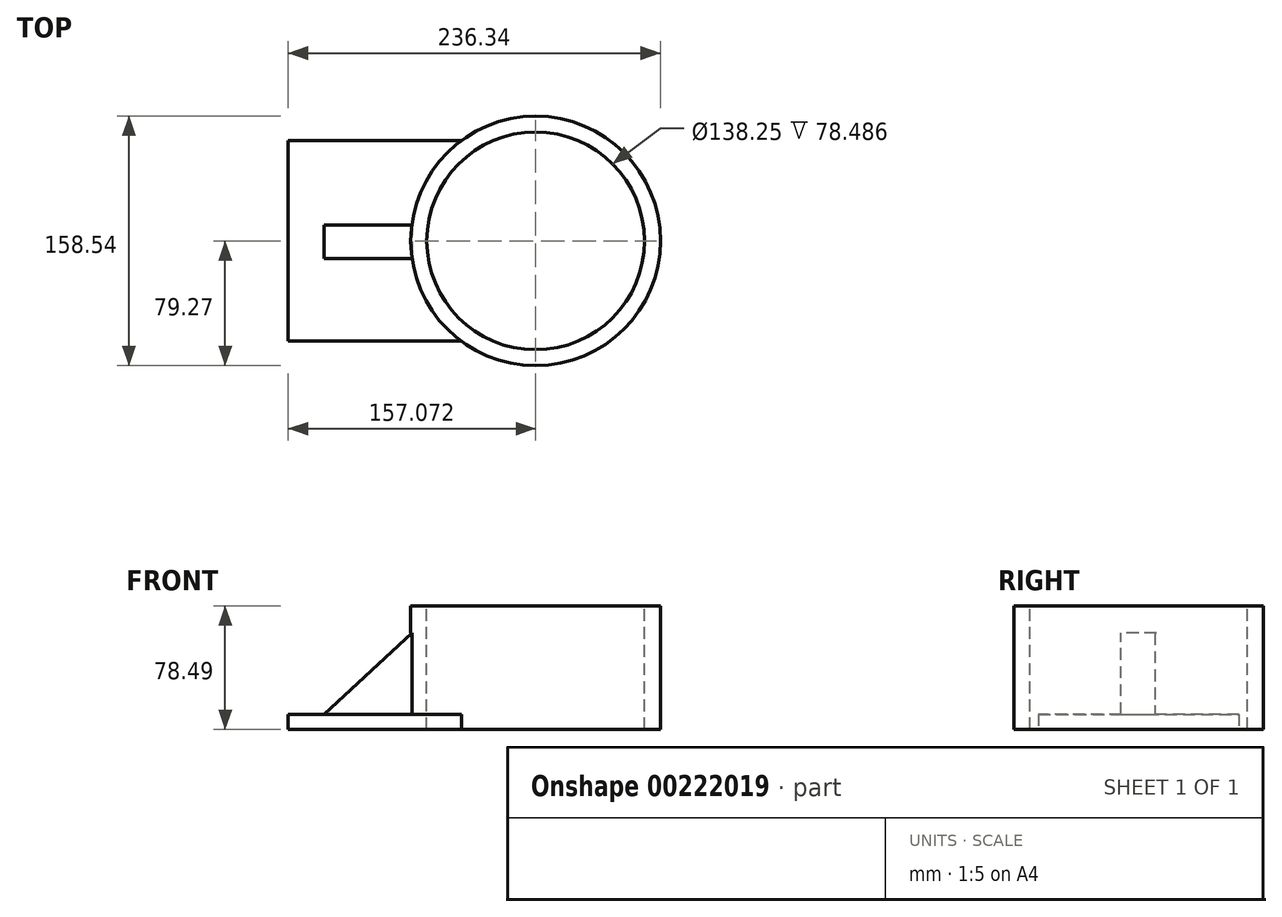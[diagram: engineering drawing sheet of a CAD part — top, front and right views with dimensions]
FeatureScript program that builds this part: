
annotation { "Feature Type Name" : "Feature", "Feature Type Description" : "" }
export const myFeature = defineFeature(function(context is Context, id is Id, definition is map)
    precondition{}
    {
        {
            var Q0;
            Q0=qCreatedBy(makeId("Top.planeOp"),FACE);
            var sketch = newSketch(context, id + "F0", { "sketchPlane" : qUnion([Q0])});
            skLineSegment(sketch, "E0.bottom", {"start": v(65.93, -63.71) * mm, "end": v(-65.93, -63.71) * mm});
            skLineSegment(sketch, "E0.top", {"start": v(65.93, 63.71) * mm, "end": v(-65.93, 63.71) * mm});
            skLineSegment(sketch, "E0.left", {"start": v(65.93, -63.71) * mm, "end": v(65.93, 63.71) * mm});
            skLineSegment(sketch, "E0.right", {"start": v(-65.93, -63.71) * mm, "end": v(-65.93, 63.71) * mm});
            skPoint(sketch, "E0.middle", {"position": v(0, 0) * mm});
            skSolve(sketch);
        }
        {
            var Q0;
            Q0=makeQuery(id+"F0.imprint","IMPRINT",FACE,{"disambiguationData":[TD([[makeQuery(id+"F0.imprint","IMPRINT",EDGE,{"derivedFrom":sQuery(id+"F0.wireOp",EDGE,"E0.bottom")}),-1.0]])]});
            extrude(context, id + "F1", {"entities" : qUnion([Q0]), "depth" : 9.65 * mm});
        }
        {
            var Q0;
            Q0=makeQuery(id+"F1.opExtrude","CAP_FACE",FACE,{"disambiguationData":[OSD([sQuery(id+"F0.wireOp",EDGE,"E0.bottom"),sQuery(id+"F0.wireOp",EDGE,"E0.top"),sQuery(id+"F0.wireOp",EDGE,"E0.left"),sQuery(id+"F0.wireOp",EDGE,"E0.right")])],"isStart":true});
            var sketch = newSketch(context, id + "F2", { "sketchPlane" : qUnion([Q0])});
            skCircle(sketch, "E1", {"center": v(91.14, 0) * mm, "radius": 79.27 * mm});
            skPoint(sketch, "E1.centerSnap0", {"position": v(65.93, 0) * mm});
            skSolve(sketch);
        }
        {
            var Q0;
            Q0 = qSketchRegion(id + "F2", true);
            extrude(context, id + "F3", {"entities" : qUnion([Q0]), "operationType" : NewBodyOperationType.ADD, "oppositeDirection" : true, "depth" : 78.49 * mm});
        }
        {
            var Q0;
            Q0=makeQuery(id+"F3.opExtrude","CAP_FACE",FACE,{"disambiguationData":[OSD([sQuery(id+"F2.wireOp",EDGE,"E1")])],"isStart":false});
            var sketch = newSketch(context, id + "F4", { "sketchPlane" : qUnion([Q0])});
            skCircle(sketch, "E2", {"center": v(91.14, 0) * mm, "radius": 69.13 * mm});
            skSolve(sketch);
        }
        {
            var Q0;
            Q0 = qSketchRegion(id + "F4", true);
            extrude(context, id + "F5", {"entities" : qUnion([Q0]), "operationType" : NewBodyOperationType.REMOVE, "oppositeDirection" : true, "depth" : 172.97 * mm});
        }
        {
            var Q0;
            Q0=makeQuery(id+"F1.opExtrude","CAP_FACE",FACE,{"disambiguationData":[OSD([sQuery(id+"F0.wireOp",EDGE,"E0.bottom"),sQuery(id+"F0.wireOp",EDGE,"E0.top"),sQuery(id+"F0.wireOp",EDGE,"E0.left"),sQuery(id+"F0.wireOp",EDGE,"E0.right")])],"isStart":false});
            var sketch = newSketch(context, id + "F6", { "sketchPlane" : qUnion([Q0])});
            skLineSegment(sketch, "E3", {"start": v(-43.1, -11.25) * mm, "end": v(12.67, -11.25) * mm});
            skLineSegment(sketch, "E4", {"start": v(-43.1, -11.25) * mm, "end": v(-43.1, 10.15) * mm});
            skLineSegment(sketch, "E5", {"start": v(-43.1, 10.15) * mm, "end": v(12.52, 10.15) * mm});
            skSolve(sketch);
        }
        {
            var Q0;
            Q0 = qSketchRegion(id + "F6", true);
            var Q1;
            {var subQ0=sQuery(id+"F6.wireOp",EDGE,"E3");Q1=makeQuery(id+"F6.imprint","IMPRINT",FACE,{"disambiguationData":[TD([[makeQuery(id+"F6.imprint","IMPRINT",EDGE,{"derivedFrom":subQ0}),1.0]])]});}
            extrude(context, id + "F7", {"entities" : qUnion([Q0, Q1]), "operationType" : NewBodyOperationType.ADD, "depth" : 51.56 * mm});
        }
        {
            var Q0;
            Q0=makeQuery(id+"F7.opExtrude","SWEPT_FACE",FACE,{"disambiguationData":[OSD([sQuery(id+"F6.wireOp",EDGE,"E3")])]});
            var sketch = newSketch(context, id + "F8", { "sketchPlane" : qUnion([Q0])});
            skLineSegment(sketch, "E6", {"start": v(-43.1, 9.65) * mm, "end": v(12.67, 61.21) * mm});
            skLineSegment(sketch, "E7", {"start": v(12.67, 61.21) * mm, "end": v(-43.1, 61.21) * mm});
            skLineSegment(sketch, "E8", {"start": v(-43.1, 61.21) * mm, "end": v(-43.1, 9.65) * mm});
            skSolve(sketch);
        }
        {
            var Q0;
            Q0 = qSketchRegion(id + "F8", true);
            extrude(context, id + "F9", {"entities" : qUnion([Q0]), "operationType" : NewBodyOperationType.REMOVE, "oppositeDirection" : true, "depth" : 25.4 * mm});
        }
    });
